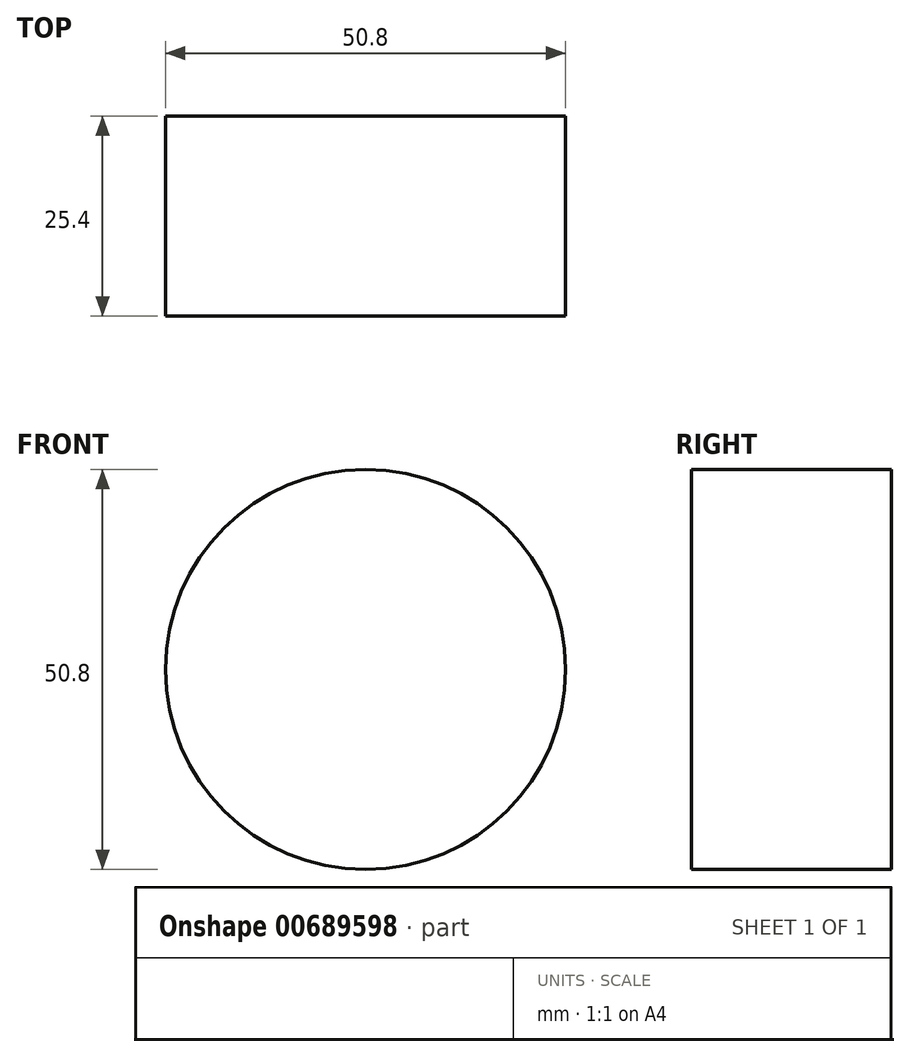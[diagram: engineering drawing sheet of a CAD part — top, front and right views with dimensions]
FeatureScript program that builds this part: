
annotation { "Feature Type Name" : "Feature", "Feature Type Description" : "" }
export const myFeature = defineFeature(function(context is Context, id is Id, definition is map)
    precondition{}
    {
        {
            var Q0;
            Q0=qCreatedBy(makeId("Front.planeOp"),FACE);
            var sketch = newSketch(context, id + "F0", { "sketchPlane" : qUnion([Q0])});
            skCircle(sketch, "E0", {"center": v(0, 0) * mm, "radius": 25.4 * mm});
            skSolve(sketch);
        }
        {
            var Q0;
            Q0 = qSketchRegion(id + "F0", true);
            extrude(context, id + "F1", {"entities" : qUnion([Q0]), "depth" : 25.4 * mm, "offsetDistance" : 25.4 * mm});
        }
    });
